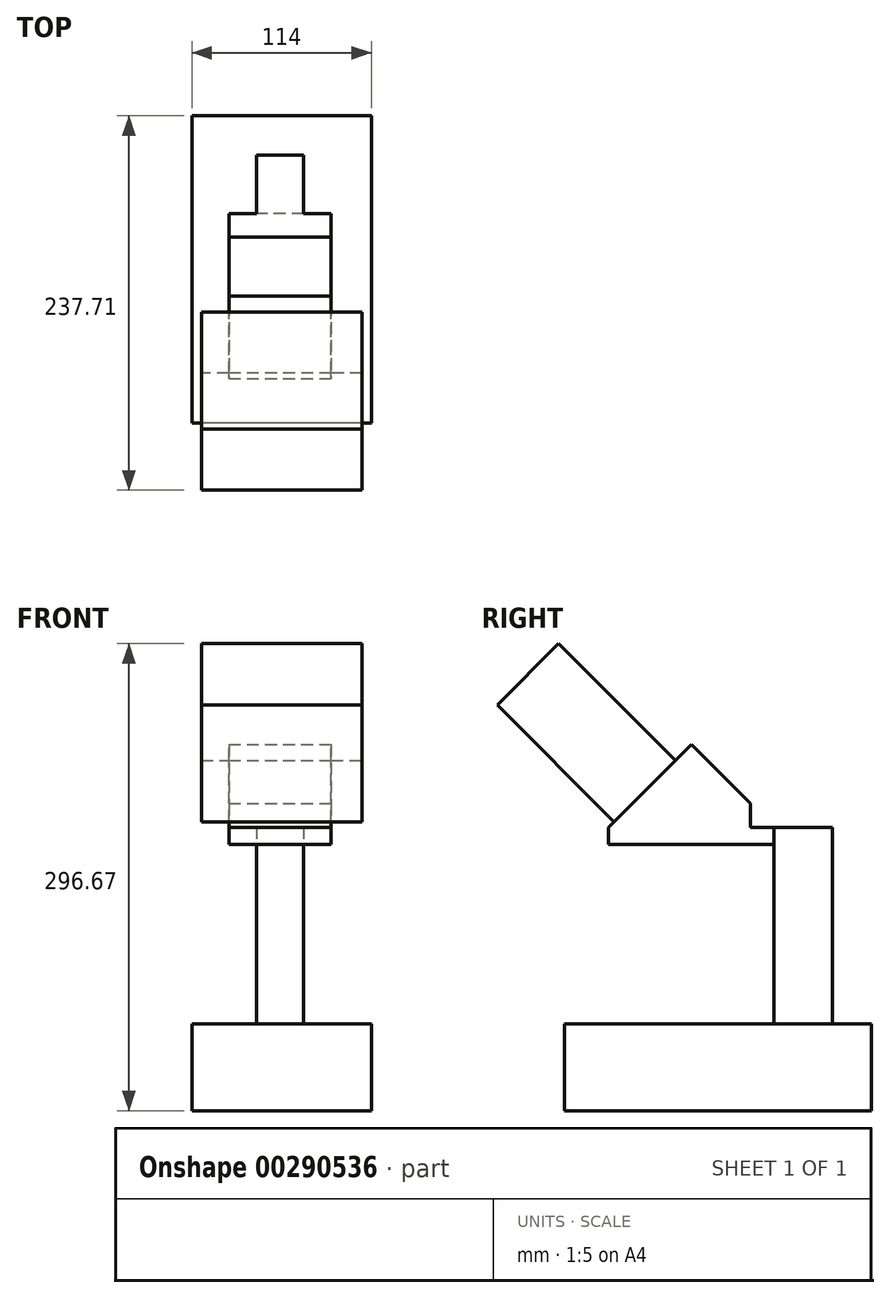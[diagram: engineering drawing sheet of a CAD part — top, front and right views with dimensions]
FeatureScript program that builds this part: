
annotation { "Feature Type Name" : "Feature", "Feature Type Description" : "" }
export const myFeature = defineFeature(function(context is Context, id is Id, definition is map)
    precondition{}
    {
        {
            var Q0;
            Q0=qCreatedBy(makeId("Top.planeOp"),FACE);
            var sketch = newSketch(context, id + "F0", { "sketchPlane" : qUnion([Q0])});
            skLineSegment(sketch, "E0.bottom", {"start": v(57, -97.5) * mm, "end": v(-57, -97.5) * mm});
            skLineSegment(sketch, "E0.top", {"start": v(57, 97.5) * mm, "end": v(-57, 97.5) * mm});
            skLineSegment(sketch, "E0.left", {"start": v(57, -97.5) * mm, "end": v(57, 97.5) * mm});
            skLineSegment(sketch, "E0.right", {"start": v(-57, -97.5) * mm, "end": v(-57, 97.5) * mm});
            skPoint(sketch, "E0.middle", {"position": v(0, 0) * mm});
            skSolve(sketch);
        }
        {
            var Q0;
            Q0 = qSketchRegion(id + "F0", true);
            extrude(context, id + "F1", {"entities" : qUnion([Q0]), "depth" : 55 * mm});
        }
        {
            var Q0;
            Q0=makeQuery(id+"F1.opExtrude","CAP_FACE",FACE,{"disambiguationData":[OSD([sQuery(id+"F0.wireOp",EDGE,"E0.bottom"),sQuery(id+"F0.wireOp",EDGE,"E0.top"),sQuery(id+"F0.wireOp",EDGE,"E0.left"),sQuery(id+"F0.wireOp",EDGE,"E0.right")])],"isStart":false});
            var sketch = newSketch(context, id + "F2", { "sketchPlane" : qUnion([Q0])});
            skLineSegment(sketch, "E1", {"start": v(57, 97.5) * mm, "end": v(57, 72.5) * mm, "construction": true});
            skLineSegment(sketch, "E2", {"start": v(57, 72.5) * mm, "end": v(14, 72.5) * mm, "construction": true});
            skLineSegment(sketch, "E3.bottom", {"start": v(14, 72.5) * mm, "end": v(-16, 72.5) * mm});
            skLineSegment(sketch, "E3.top", {"start": v(14, 35.5) * mm, "end": v(-16, 35.5) * mm});
            skLineSegment(sketch, "E3.left", {"start": v(14, 72.5) * mm, "end": v(14, 35.5) * mm});
            skLineSegment(sketch, "E3.right", {"start": v(-16, 72.5) * mm, "end": v(-16, 35.5) * mm});
            skSolve(sketch);
        }
        {
            var Q0;
            Q0 = qSketchRegion(id + "F2", true);
            extrude(context, id + "F3", {"entities" : qUnion([Q0]), "operationType" : NewBodyOperationType.ADD, "depth" : 125 * mm});
        }
        {
            var Q0;
            Q0=makeQuery(id+"F3.opExtrude","CAP_FACE",FACE,{"disambiguationData":[OSD([sQuery(id+"F2.wireOp",EDGE,"E3.bottom"),sQuery(id+"F2.wireOp",EDGE,"E3.top"),sQuery(id+"F2.wireOp",EDGE,"E3.left"),sQuery(id+"F2.wireOp",EDGE,"E3.right")])],"isStart":false});
            var sketch = newSketch(context, id + "F4", { "sketchPlane" : qUnion([Q0])});
            skLineSegment(sketch, "E4", {"start": v(-1, 35.5) * mm, "end": v(-33.5, 35.5) * mm});
            skLineSegment(sketch, "E5", {"start": v(-33.5, 35.5) * mm, "end": v(-33.5, -69.5) * mm});
            skLineSegment(sketch, "E6", {"start": v(-33.5, -69.5) * mm, "end": v(-1, -69.5) * mm});
            skLineSegment(sketch, "E7", {"start": v(-1, -69.5) * mm, "end": v(-1, 35.5) * mm, "construction": true});
            skLineSegment(sketch, "E8.MirrorCS", {"start": v(-1, 35.5) * mm, "end": v(31.5, 35.5) * mm});
            skLineSegment(sketch, "E9.MirrorCS", {"start": v(31.5, 35.5) * mm, "end": v(31.5, -69.5) * mm});
            skLineSegment(sketch, "E10.MirrorCS", {"start": v(31.5, -69.5) * mm, "end": v(-1, -69.5) * mm});
            skSolve(sketch);
        }
        {
            var Q0;
            {var subQ3=sQuery(id+"F4.wireOp",EDGE,"E5");Q0=makeQuery(id+"F4.imprint","IMPRINT",FACE,{"disambiguationData":[TD([[makeQuery(id+"F4.imprint","IMPRINT",EDGE,{"derivedFrom":subQ3}),1.0]])]});}
            extrude(context, id + "F5", {"entities" : qUnion([Q0]), "operationType" : NewBodyOperationType.ADD, "oppositeDirection" : true, "depth" : 11 * mm});
        }
        {
            var Q0;
            Q0=makeQuery(id+"F5.opExtrude","SWEPT_FACE",FACE,{"disambiguationData":[OSD([sQuery(id+"F4.wireOp",EDGE,"E9.MirrorCS")])]});
            var sketch = newSketch(context, id + "F6", { "sketchPlane" : qUnion([Q0])});
            skLineSegment(sketch, "E11", {"start": v(-69.5, 180) * mm, "end": v(-17, 180) * mm, "construction": true});
            skLineSegment(sketch, "E12", {"start": v(-17, 180) * mm, "end": v(-17, 232.5) * mm, "construction": true});
            skLineSegment(sketch, "E13", {"start": v(-69.5, 180) * mm, "end": v(-17, 232.5) * mm});
            skLineSegment(sketch, "E14", {"start": v(35.5, 180) * mm, "end": v(20.5, 180) * mm, "construction": true});
            skLineSegment(sketch, "E15", {"start": v(-17, 232.5) * mm, "end": v(35.5, 180) * mm, "construction": true});
            skLineSegment(sketch, "E16", {"start": v(20.5, 180) * mm, "end": v(20.5, 195) * mm, "construction": true});
            skLineSegment(sketch, "E17", {"start": v(-17, 232.5) * mm, "end": v(20.5, 195) * mm});
            skLineSegment(sketch, "E18", {"start": v(20.5, 195) * mm, "end": v(20.5, 180) * mm});
            skLineSegment(sketch, "E19", {"start": v(20.5, 180) * mm, "end": v(-69.5, 180) * mm});
            skSolve(sketch);
        }
        {
            var Q0;
            Q0 = qSketchRegion(id + "F6", true);
            var Q1;
            Q1=makeQuery(id+"F5.opExtrude","SWEPT_FACE",FACE,{"disambiguationData":[OSD([sQuery(id+"F4.wireOp",EDGE,"E5")])]});
            extrude(context, id + "F7", {"entities" : qUnion([Q0]), "operationType" : NewBodyOperationType.ADD, "endBound" : BoundingType.UP_TO_SURFACE, "oppositeDirection" : true, "endBoundEntityFace" : qUnion([Q1]), "depth" : 25 * mm});
        }
        {
            var Q0;
            Q0=makeQuery(id+"F7.opExtrude","SWEPT_FACE",FACE,{"disambiguationData":[OSD([sQuery(id+"F6.wireOp",EDGE,"E13")])]});
            var sketch = newSketch(context, id + "F8", { "sketchPlane" : qUnion([Q0])});
            skLineSegment(sketch, "E20", {"start": v(-33.5, 78.14) * mm, "end": v(-33.5, 83.14) * mm, "construction": true});
            skLineSegment(sketch, "E21", {"start": v(-33.5, 83.14) * mm, "end": v(-51, 83.14) * mm});
            skLineSegment(sketch, "E22", {"start": v(-51, 83.14) * mm, "end": v(-51, 138.14) * mm});
            skLineSegment(sketch, "E23", {"start": v(-51, 138.14) * mm, "end": v(0, 138.14) * mm});
            skLineSegment(sketch, "E24", {"start": v(0, 138.14) * mm, "end": v(0, 78.14) * mm, "construction": true});
            skLineSegment(sketch, "E25", {"start": v(-33.5, 83.14) * mm, "end": v(0, 83.14) * mm});
            skLineSegment(sketch, "E26.MirrorCS", {"start": v(51, 138.14) * mm, "end": v(0, 138.14) * mm});
            skLineSegment(sketch, "E27.MirrorCS", {"start": v(51, 83.14) * mm, "end": v(51, 138.14) * mm});
            skLineSegment(sketch, "E28.MirrorCS", {"start": v(33.5, 83.14) * mm, "end": v(0, 83.14) * mm});
            skLineSegment(sketch, "E29.MirrorCS", {"start": v(33.5, 83.14) * mm, "end": v(51, 83.14) * mm});
            skSolve(sketch);
        }
        {
            var Q0;
            Q0 = qSketchRegion(id + "F8", true);
            extrude(context, id + "F9", {"entities" : qUnion([Q0]), "operationType" : NewBodyOperationType.ADD, "depth" : 105 * mm});
        }
    });
